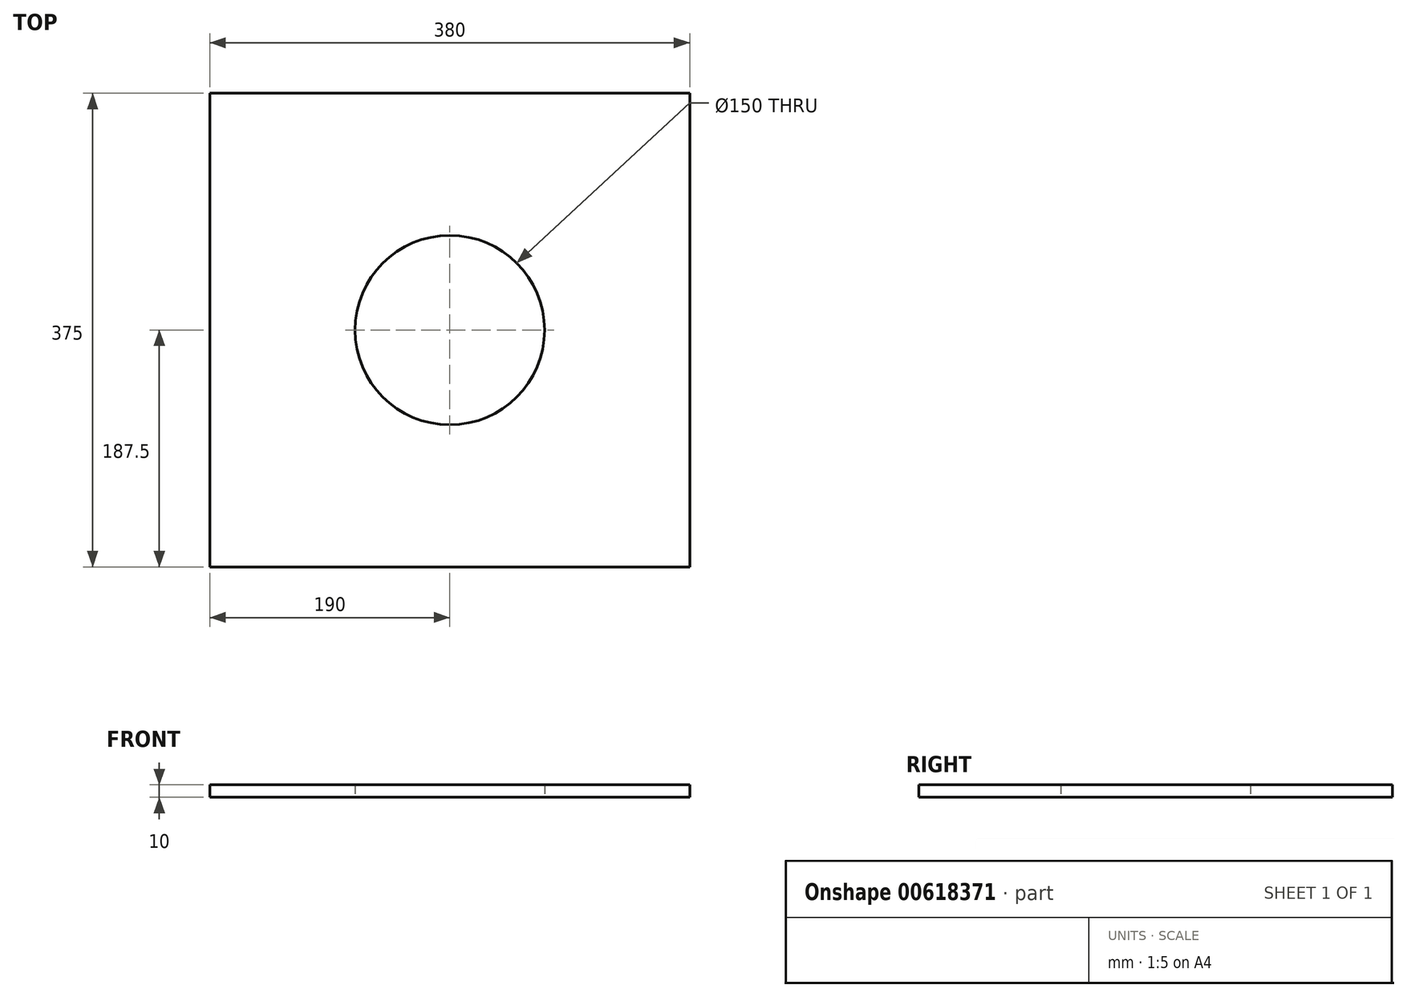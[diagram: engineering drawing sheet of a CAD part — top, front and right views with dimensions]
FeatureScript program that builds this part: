
annotation { "Feature Type Name" : "Feature", "Feature Type Description" : "" }
export const myFeature = defineFeature(function(context is Context, id is Id, definition is map)
    precondition{}
    {
        {
            var Q0;
            Q0=qCreatedBy(makeId("Top.planeOp"),FACE);
            var sketch = newSketch(context, id + "F0", { "sketchPlane" : qUnion([Q0])});
            skLineSegment(sketch, "E0.bottom", {"start": v(190, -187.5) * mm, "end": v(-190, -187.5) * mm});
            skLineSegment(sketch, "E0.top", {"start": v(190, 187.5) * mm, "end": v(-190, 187.5) * mm});
            skLineSegment(sketch, "E0.left", {"start": v(190, -187.5) * mm, "end": v(190, 187.5) * mm});
            skLineSegment(sketch, "E0.right", {"start": v(-190, -187.5) * mm, "end": v(-190, 187.5) * mm});
            skPoint(sketch, "E0.middle", {"position": v(0, 0) * mm});
            skCircle(sketch, "E1", {"center": v(0, 0) * mm, "radius": 75 * mm});
            skSolve(sketch);
        }
        {
            var Q0;
            Q0=makeQuery(id+"F0.imprint","IMPRINT",FACE,{"disambiguationData":[TD([[makeQuery(id+"F0.imprint","IMPRINT",EDGE,{"derivedFrom":sQuery(id+"F0.wireOp",EDGE,"E0.bottom")}),-1.0]])]});
            extrude(context, id + "F1", {"entities" : qUnion([Q0]), "depth" : 5 * mm, "offsetDistance" : 25 * mm, "hasSecondDirection" : true, "secondDirectionOppositeDirection" : true, "secondDirectionDepth" : 5 * mm});
        }
    });
